# Revit family: P6397-30
name_source: partatom
category: Lighting Fixtures
revit_build: Autodesk Revit 2014 (Build: 20130308_1515(x64)
units: mm (PartAtom-declared; Revit-internal decimal feet)

## types (1)
- INT
    Angle Tilt = 65°
    Apparent Load = 250 VA
    Assembly Code = D5020200
    Black = Paint - Hubbell - Basic Black Textured
    Connector Description = Lighting Connector
    Default Elevation = 48 "
    Description = One-Light Multi Directional Wall/Ceiling Heat Lamp
    Fixture distribution = Direct
    Glass = Hubbell - Glass
    Height = 2.5 "
    Housing Material = Paint - Hubbell - White Texture
    Lamp = Incandescent
    Length = 24 "
    Load Classification = Lighting
    Manufacturer = Progress Lighting
    Model = P6397-30
    Mounting = Paint - Hubbell - Light Silver
    Power Factor = 1
    Product Documentation URL = https://hubbellcdn.com
    Product Page URL = https://www.hubbell.com
    Reflector Finish = Hubbell - White Glass
    URL = https://www.hubbell.com
    Voltage = 120 V
    Warranty = year Warranty
    Wattage Comments = 250W
    Watts = 250 W
    Width = 3.875 "
    Wings = Paint - Hubbell - Light Silver
    zz Angle = 65°

## geometry (parser evidence)
native form markers: Sweep x7
no freeform markers — native parametric forms only
